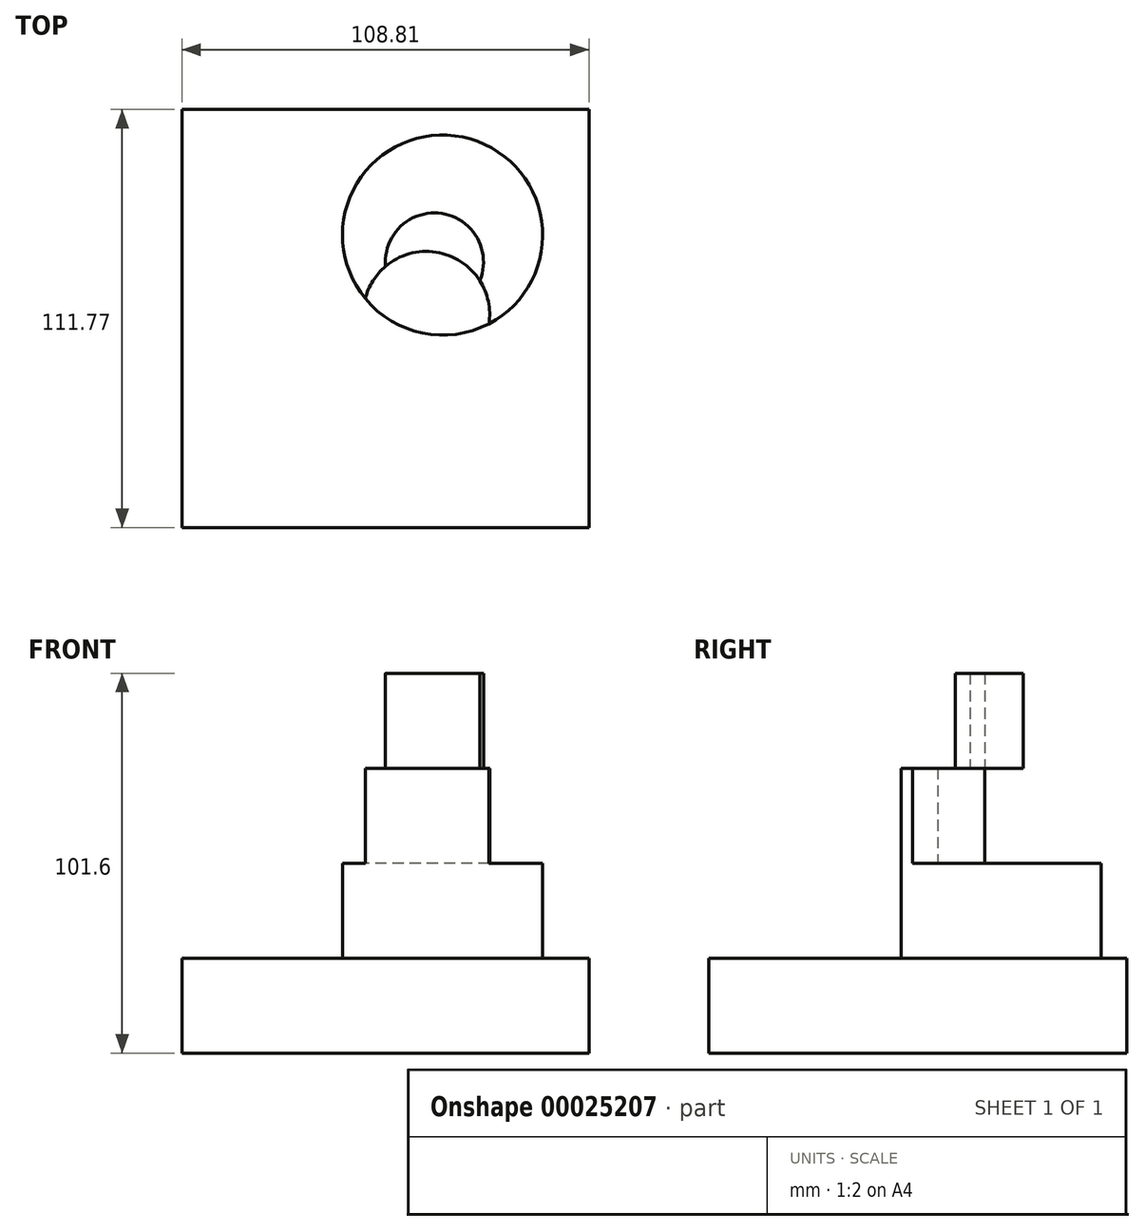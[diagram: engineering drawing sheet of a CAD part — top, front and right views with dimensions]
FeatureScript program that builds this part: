
annotation { "Feature Type Name" : "Feature", "Feature Type Description" : "" }
export const myFeature = defineFeature(function(context is Context, id is Id, definition is map)
    precondition{}
    {
        {
            var Q0;
            Q0=qCreatedBy(makeId("Top.planeOp"),FACE);
            var sketch = newSketch(context, id + "F0", { "sketchPlane" : qUnion([Q0])});
            skLineSegment(sketch, "E0.bottom", {"start": v(49.1, -56.92) * mm, "end": v(-59.7, -56.92) * mm});
            skLineSegment(sketch, "E0.top", {"start": v(49.1, 54.85) * mm, "end": v(-59.7, 54.85) * mm});
            skLineSegment(sketch, "E0.left", {"start": v(49.1, -56.92) * mm, "end": v(49.1, 54.85) * mm});
            skLineSegment(sketch, "E0.right", {"start": v(-59.7, -56.92) * mm, "end": v(-59.7, 54.85) * mm});
            skSolve(sketch);
        }
        {
            var Q0;
            Q0 = qSketchRegion(id + "F0", true);
            extrude(context, id + "F1", {"entities" : qUnion([Q0]), "depth" : 25.4 * mm});
        }
        {
            var Q0;
            Q0=makeQuery(id+"F1.opExtrude","CAP_FACE",FACE,{"disambiguationData":[OSD([sQuery(id+"F0.wireOp",EDGE,"E0.bottom"),sQuery(id+"F0.wireOp",EDGE,"E0.top"),sQuery(id+"F0.wireOp",EDGE,"E0.left"),sQuery(id+"F0.wireOp",EDGE,"E0.right")])],"isStart":false});
            var sketch = newSketch(context, id + "F2", { "sketchPlane" : qUnion([Q0])});
            skCircle(sketch, "E1", {"center": v(9.96, 21.27) * mm, "radius": 26.76 * mm});
            skSolve(sketch);
        }
        {
            var Q0;
            Q0=makeQuery(id+"F2.imprint","IMPRINT",FACE,{"disambiguationData":[TD([[makeQuery(id+"F2.imprint","IMPRINT",EDGE,{"derivedFrom":sQuery(id+"F2.wireOp",EDGE,"E1")}),1.0]])]});
            extrude(context, id + "F3", {"entities" : qUnion([Q0]), "operationType" : NewBodyOperationType.ADD, "depth" : 25.4 * mm});
        }
        {
            var Q0;
            Q0=makeQuery(id+"F3.opExtrude","CAP_FACE",FACE,{"disambiguationData":[OSD([sQuery(id+"F2.wireOp",EDGE,"E1")])],"isStart":false});
            var sketch = newSketch(context, id + "F4", { "sketchPlane" : qUnion([Q0])});
            skCircle(sketch, "E2", {"center": v(5.63, 0) * mm, "radius": 16.92 * mm});
            skSolve(sketch);
        }
        {
            var Q0;
            {var subQ0=makeQuery(id+"F3.opExtrude","CAP_EDGE",EDGE,{"disambiguationData":[OSD([sQuery(id+"F2.wireOp",EDGE,"E1")])],"isStart":false});var subQ1=sQuery(id+"F4.wireOp",EDGE,"E2");var subQ3=makeQuery(id+"F4.imprint","INTERSECT",VERTEX,{"disambiguationData":[OD(0.0)],"derivedFrom":[subQ0,subQ1]});Q0=makeQuery(id+"F4.imprint","IMPRINT",FACE,{"disambiguationData":[TD([[makeQuery(id+"F4.imprint","IMPRINT",EDGE,{"disambiguationData":[TD([[subQ3,1.0]])],"derivedFrom":subQ1}),1.0]])]});}
            extrude(context, id + "F5", {"entities" : qUnion([Q0]), "operationType" : NewBodyOperationType.ADD, "depth" : 25.4 * mm});
        }
        {
            var Q0;
            Q0=makeQuery(id+"F5.opExtrude","CAP_FACE",FACE,{"disambiguationData":[OSD([sQuery(id+"F2.wireOp",EDGE,"E1"),sQuery(id+"F4.wireOp",EDGE,"E2")])],"isStart":false});
            var sketch = newSketch(context, id + "F6", { "sketchPlane" : qUnion([Q0])});
            skSolve(sketch);
        }
        {
            var Q0;
            Q0=makeQuery(id+"F6.imprint","IMPRINT",FACE,{"disambiguationData":[TD([[makeQuery(id+"F6.imprint","IMPRINT",EDGE,{"derivedFrom":makeQuery(id+"F5.opExtrude","CAP_EDGE",EDGE,{"disambiguationData":[OSD([sQuery(id+"F4.wireOp",EDGE,"E2")])],"isStart":false})}),1.0]])]});
            var sketch = newSketch(context, id + "F7", { "sketchPlane" : qUnion([Q0])});
            skCircle(sketch, "E3", {"center": v(7.78, 14.09) * mm, "radius": 13.12 * mm});
            skSolve(sketch);
        }
        {
            var Q0;
            {var subQ0=makeQuery(id+"F6.imprint","IMPRINT",EDGE,{"derivedFrom":makeQuery(id+"F5.opExtrude","CAP_EDGE",EDGE,{"disambiguationData":[OSD([sQuery(id+"F4.wireOp",EDGE,"E2")])],"isStart":false})});var subQ1=sQuery(id+"F7.wireOp",EDGE,"E3");var subQ3=makeQuery(id+"F7.imprint","INTERSECT",VERTEX,{"disambiguationData":[OD(0.0)],"derivedFrom":[subQ0,subQ1]});Q0=makeQuery(id+"F7.imprint","IMPRINT",FACE,{"disambiguationData":[TD([[makeQuery(id+"F7.imprint","IMPRINT",EDGE,{"disambiguationData":[TD([[subQ3,1.0]])],"derivedFrom":subQ1}),1.0]])]});}
            extrude(context, id + "F8", {"entities" : qUnion([Q0]), "depth" : 25.4 * mm});
        }
    });
